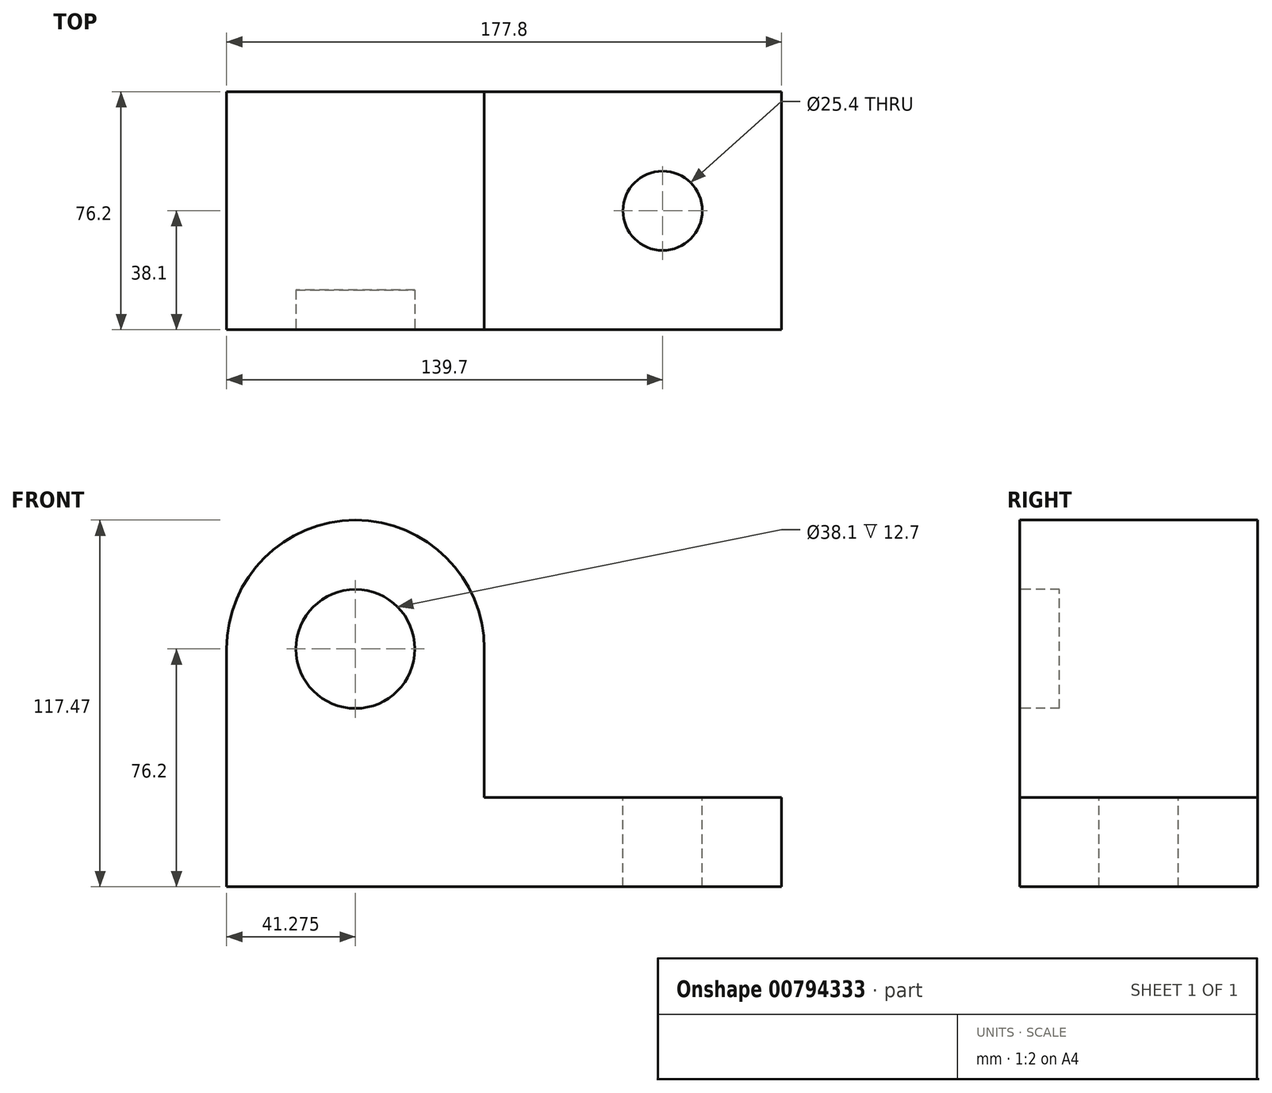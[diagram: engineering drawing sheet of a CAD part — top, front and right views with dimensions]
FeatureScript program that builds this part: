
annotation { "Feature Type Name" : "Feature", "Feature Type Description" : "" }
export const myFeature = defineFeature(function(context is Context, id is Id, definition is map)
    precondition{}
    {
        {
            var Q0;
            Q0=qCreatedBy(makeId("Front.planeOp"),FACE);
            var sketch = newSketch(context, id + "F0", { "sketchPlane" : qUnion([Q0])});
            skLineSegment(sketch, "E0", {"start": v(0, 0) * mm, "end": v(177.8, 0) * mm});
            skLineSegment(sketch, "E1", {"start": v(177.8, 0) * mm, "end": v(177.8, 28.58) * mm});
            skLineSegment(sketch, "E2", {"start": v(177.8, 28.58) * mm, "end": v(82.55, 28.58) * mm});
            skLineSegment(sketch, "E3", {"start": v(82.55, 28.58) * mm, "end": v(82.55, 155.57) * mm});
            skLineSegment(sketch, "E4", {"start": v(82.55, 155.57) * mm, "end": v(0, 155.57) * mm});
            skLineSegment(sketch, "E5", {"start": v(0, 155.57) * mm, "end": v(0, 0) * mm});
            skSolve(sketch);
        }
        {
            var Q0;
            Q0=makeQuery(id+"F0.imprint","IMPRINT",FACE,{"disambiguationData":[TD([[makeQuery(id+"F0.imprint","IMPRINT",EDGE,{"derivedFrom":sQuery(id+"F0.wireOp",EDGE,"E0")}),1.0]])]});
            extrude(context, id + "F1", {"entities" : qUnion([Q0]), "depth" : 76.2 * mm, "offsetDistance" : 25.4 * mm});
        }
        {
            var Q0;
            Q0=makeQuery(id+"F1.opExtrude","CAP_FACE",FACE,{"disambiguationData":[OSD([sQuery(id+"F0.wireOp",EDGE,"E0"),sQuery(id+"F0.wireOp",EDGE,"E1"),sQuery(id+"F0.wireOp",EDGE,"E2"),sQuery(id+"F0.wireOp",EDGE,"E3"),sQuery(id+"F0.wireOp",EDGE,"E4"),sQuery(id+"F0.wireOp",EDGE,"E5")])],"isStart":false});
            var sketch = newSketch(context, id + "F2", { "sketchPlane" : qUnion([Q0])});
            skLineSegment(sketch, "E6", {"start": v(0, 0) * mm, "end": v(0, 76.2) * mm});
            skLineSegment(sketch, "E7", {"start": v(82.55, 28.58) * mm, "end": v(82.55, 76.2) * mm});
            skLineSegment(sketch, "E8", {"start": v(82.55, 76.2) * mm, "end": v(0, 76.2) * mm, "construction": true});
            skArc(sketch, "E9", {"start": v(82.55, 76.2) * mm, "mid": v(41.27, 117.48) * mm, "end": v(0, 76.2) * mm});
            skCircle(sketch, "E10", {"center": v(41.27, 76.2) * mm, "radius": 19.05 * mm});
            skSolve(sketch);
        }
        {
            var Q0;
            Q0=makeQuery(id+"F2.imprint","IMPRINT",FACE,{"disambiguationData":[TD([[makeQuery(id+"F2.imprint","IMPRINT",EDGE,{"derivedFrom":sQuery(id+"F2.wireOp",EDGE,"E10")}),1.0]])]});
            extrude(context, id + "F3", {"entities" : qUnion([Q0]), "operationType" : NewBodyOperationType.REMOVE, "oppositeDirection" : true, "depth" : 12.7 * mm, "offsetDistance" : 25.4 * mm});
        }
        {
            var Q0;
            {var subQ0=sQuery(id+"F2.wireOp",EDGE,"E9");Q0=makeQuery(id+"F2.imprint","IMPRINT",FACE,{"disambiguationData":[TD([[makeQuery(id+"F2.imprint","IMPRINT",EDGE,{"derivedFrom":subQ0}),-1.0]])]});}
            extrude(context, id + "F4", {"entities" : qUnion([Q0]), "operationType" : NewBodyOperationType.REMOVE, "oppositeDirection" : true, "depth" : 76.2 * mm, "offsetDistance" : 25.4 * mm});
        }
        {
            var Q0;
            Q0=makeQuery(id+"F1.opExtrude","SWEPT_FACE",FACE,{"disambiguationData":[OSD([sQuery(id+"F0.wireOp",EDGE,"E2")])]});
            var sketch = newSketch(context, id + "F5", { "sketchPlane" : qUnion([Q0])});
            skLineSegment(sketch, "E11", {"start": v(177.8, 0) * mm, "end": v(139.7, 0) * mm});
            skLineSegment(sketch, "E12", {"start": v(139.7, 0) * mm, "end": v(139.7, -76.2) * mm, "construction": true});
            skCircle(sketch, "E13", {"center": v(139.7, -38.1) * mm, "radius": 12.7 * mm});
            skSolve(sketch);
        }
        {
            var Q0;
            Q0=makeQuery(id+"F5.imprint","IMPRINT",FACE,{"disambiguationData":[TD([[makeQuery(id+"F5.imprint","IMPRINT",EDGE,{"derivedFrom":sQuery(id+"F5.wireOp",EDGE,"E13")}),1.0]])]});
            extrude(context, id + "F6", {"entities" : qUnion([Q0]), "operationType" : NewBodyOperationType.REMOVE, "oppositeDirection" : true, "depth" : 25374.6 * mm, "offsetDistance" : 25.4 * mm});
        }
    });
